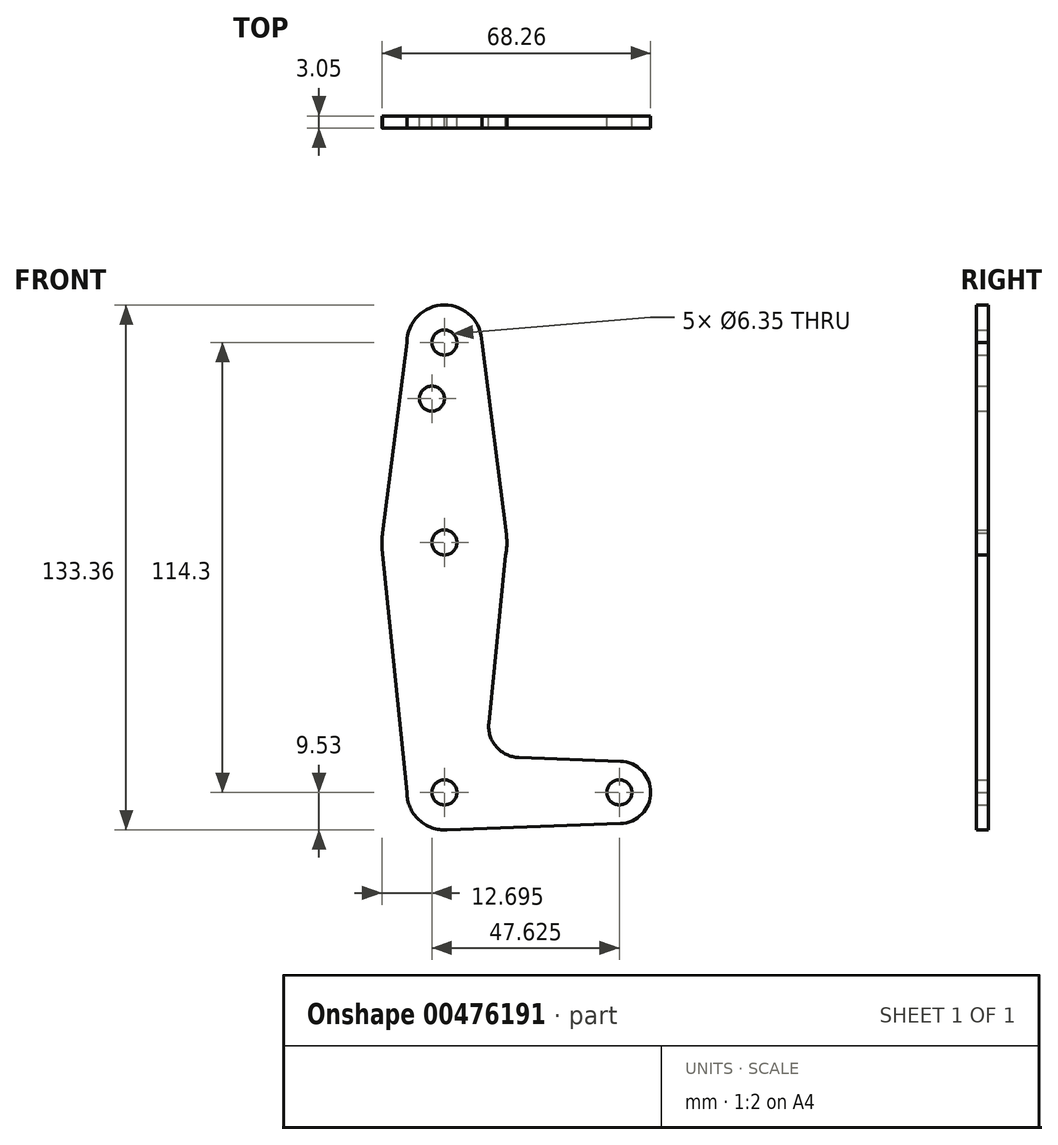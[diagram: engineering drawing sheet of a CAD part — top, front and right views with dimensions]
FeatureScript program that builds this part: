
annotation { "Feature Type Name" : "Feature", "Feature Type Description" : "" }
export const myFeature = defineFeature(function(context is Context, id is Id, definition is map)
    precondition{}
    {
        {
            var Q0;
            Q0=qCreatedBy(makeId("Front.planeOp"),FACE);
            var sketch = newSketch(context, id + "F0", { "sketchPlane" : qUnion([Q0])});
            skLineSegment(sketch, "E0", {"start": v(0, 0) * mm, "end": v(0, 114.3) * mm, "construction": true});
            skLineSegment(sketch, "E1", {"start": v(0, 0) * mm, "end": v(44.45, 0) * mm, "construction": true});
            skCircle(sketch, "E2", {"center": v(0, 114.3) * mm, "radius": 9.53 * mm});
            skCircle(sketch, "E3", {"center": v(0, 63.5) * mm, "radius": 15.88 * mm});
            skCircle(sketch, "E4", {"center": v(0, 0) * mm, "radius": 9.53 * mm});
            skCircle(sketch, "E5", {"center": v(44.45, 0) * mm, "radius": 7.94 * mm});
            skLineSegment(sketch, "E6", {"start": v(-9.53, 0) * mm, "end": v(-15.8, 61.9) * mm});
            skLineSegment(sketch, "E7", {"start": v(0, -9.53) * mm, "end": v(44.73, -7.93) * mm});
            skLineSegment(sketch, "E8", {"start": v(18.91, 8.85) * mm, "end": v(44.73, 7.93) * mm});
            skLineSegment(sketch, "E9", {"start": v(11.28, 17.59) * mm, "end": v(15.88, 63.5) * mm});
            skLineSegment(sketch, "E10", {"start": v(-9.53, 114.3) * mm, "end": v(-15.8, 65.1) * mm});
            skLineSegment(sketch, "E11", {"start": v(9.53, 114.3) * mm, "end": v(15.75, 65.5) * mm});
            skCircle(sketch, "E12", {"center": v(0, 63.5) * mm, "radius": 3.18 * mm});
            skCircle(sketch, "E13", {"center": v(0, 0) * mm, "radius": 3.18 * mm});
            skCircle(sketch, "E14", {"center": v(44.45, 0) * mm, "radius": 3.18 * mm});
            skCircle(sketch, "E15", {"center": v(0, 114.3) * mm, "radius": 3.18 * mm});
            skCircle(sketch, "E16", {"center": v(-3.18, 100.03) * mm, "radius": 3.18 * mm});
            skArc(sketch, "E17.filletArc", {"start": v(11.28, 17.59) * mm, "mid": v(13.2, 11.57) * mm, "end": v(18.91, 8.85) * mm});
            skSolve(sketch);
        }
        {
            var Q0;
            Q0 = qSketchRegion(id + "F0", true);
            extrude(context, id + "F1", {"entities" : qUnion([Q0]), "depth" : 3.05 * mm});
        }
    });
